# Revit family: IS_IdealrainPro_B9846_BIM_FR
name_source: partatom
category: Plumbing Fixtures
revit_build: Autodesk Revit 2017 (Build: 20160225_1515(x64)
units: mm (PartAtom-declared; Revit-internal decimal feet)

## family parameters
Always vertical = No
Cut with Voids When Loaded = No
OmniClass Number = 23.45.05.14.21.11
OmniClass Title = Bath/Shower Units
Part Type = Normal
Room Calculation Point = No
Round Connector Dimension = Use Diameter
Shared = No
Work Plane-Based = No

## types (1)
- B9846AA - IDEALRAIN PRO SUPPORT FIX MURALE FIXE
    Accessoires = www.idealstandard.be
    Auteur = Ideal Standard
    BOSUseNativeGeometries = 1
    Bim-NomDuProjet = ISI_IdealStandard_ShowerFittingsPackage_IdealrainPro_B9846
    Caractéristiques = IDEALRAIN PRO Support mural fixe
    CodeBarre = 3800861030225
    ConseilsDInstallation = www.idealstandard.be
    Cost = 0 $
    Couleur = Chrome
    CoûtDeRemplacement = 0
    DateDeCréation = 2018_08_15
    Description = IDEALRAIN PRO Support mural fixe
    Dimensions = 80 x 64 x 45 mm
    Espace = Interne
    Finition = Chrome
    Forme = sculpté
    Hauteur = 45 mm  [stored 0.147638 ft]
    IfcExportAs = Shower fittings package
    IfcExportType = IfcSanitaryTerminalType
    InformationsProduit = www.idealstandard.be
    Largeur = 80 mm
    LienUtile = www.idealstandard.be
    Longueur = 63 mm
    Manufacturer = www.idealstandard.be
    Marque = Ideal Standard
    Matériel = 0
    Model = B9846AA
    Nom = ShowerFittingsPackage_IdealrainPro_B9846_IdealStandard
    PoidsNet = 0,23 KG
    Profondeur = 0 mm  [stored 0 ft]
    Raccordement = Plomberie
    Révision = 1
    URL = www.idealstandard.be
    Uniclass2015Code = Pr_40_20_87_75
    Uniclass2015Title = Shower fittings package
    Uniclass2015Version = Products v1.1
    UnitéDeMesure = Millimètres
    UnitéDeTemps = An
    UnitéMonétaire = €
    UrlDuFabricant = www.idealstandard.be
    Version = 1

note: [stored X ft] marks values corroborated as IEEE doubles in the binary element streams (Revit-internal decimal feet)

## geometry (parser evidence)
native form markers: Sweep x2
no freeform markers — native parametric forms only
